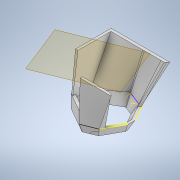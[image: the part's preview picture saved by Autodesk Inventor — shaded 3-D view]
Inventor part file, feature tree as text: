
AUTODESK INVENTOR PART (.ipt)
format: ipt  version: 2022 (Build 260153000, 153)  size: 330,240 bytes
history: native  units: in
note: dims shown in document units (in); Inventor stores cm internally (conversion verified against a paired STEP export)
features: sketch x6, plane x4, loft x3, extrude x1, split x1
ambient origin geometry x8: Origin, YZ Plane, XZ Plane, XY Plane, X Axis, Y Axis, Z Axis, Center Point
bodies: Solid1 (feature_tree)
feature tree (15):
  sketch  "Sketch1"  dims[d0=0.2441in d1=60.0deg]
  plane  "Work Plane1"
  plane  "Work Plane2"
  sketch  "Sketch2"  dims[d2=0.1063in d3=0.202in]
  loft  "Loft1"
  extrude  "Extrusion3"  Depth=0.202in
  sketch  "Sketch4"  dims[d8=0.0315in d11=0.1181in]
  plane  "Work Plane3"
  split  "Split3"
  sketch  "Sketch5"  dims[d14=0.0315in]
  plane  "Work Plane4"
  sketch  "Sketch6"  dims[d15=0.0315in d16=0.0in d17=90.0deg d18=0.0in d19=90.0deg d20=0.1181in d27=0.0394in d28=0.1181in d29=0.0in d30=0.0in d31=-0.0276in d33=0.3937in d34=0.4331in d36=0.0315in d39=0.0315in d40=0.6299in d44=0.3543in d45=0.7087in d48=0.0315in d57=0.0in d58=90.0deg d59=0.0in d60=90.0deg d61=0.0in d62=90.0deg d63=0.0in d64=90.0deg]
  loft  "Loft3"
  loft  "Loft4"
  sketch  "Sketch3"  dims[d4=0.1181in d7=0.0315in]
